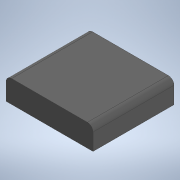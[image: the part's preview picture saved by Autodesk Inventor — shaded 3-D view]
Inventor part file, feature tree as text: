
AUTODESK INVENTOR PART (.ipt)
format: ipt  version: 2020 (Build 240168000, 168)  size: 102,912 bytes
history: native  units: mm
features: extrude x1, sketch x1
ambient origin geometry x8: Origin, YZ Plane, XZ Plane, XY Plane, X Axis, Y Axis, Z Axis, Center Point
bodies: Solid1 (feature_tree)
feature tree (2):
  extrude  "Extrusion1"  Depth=62.0mm
  sketch  "Sketch1"  dims[d0=16.0mm d1=62.0mm d2=4.0mm d3=57.7mm d4=0.0mm]
